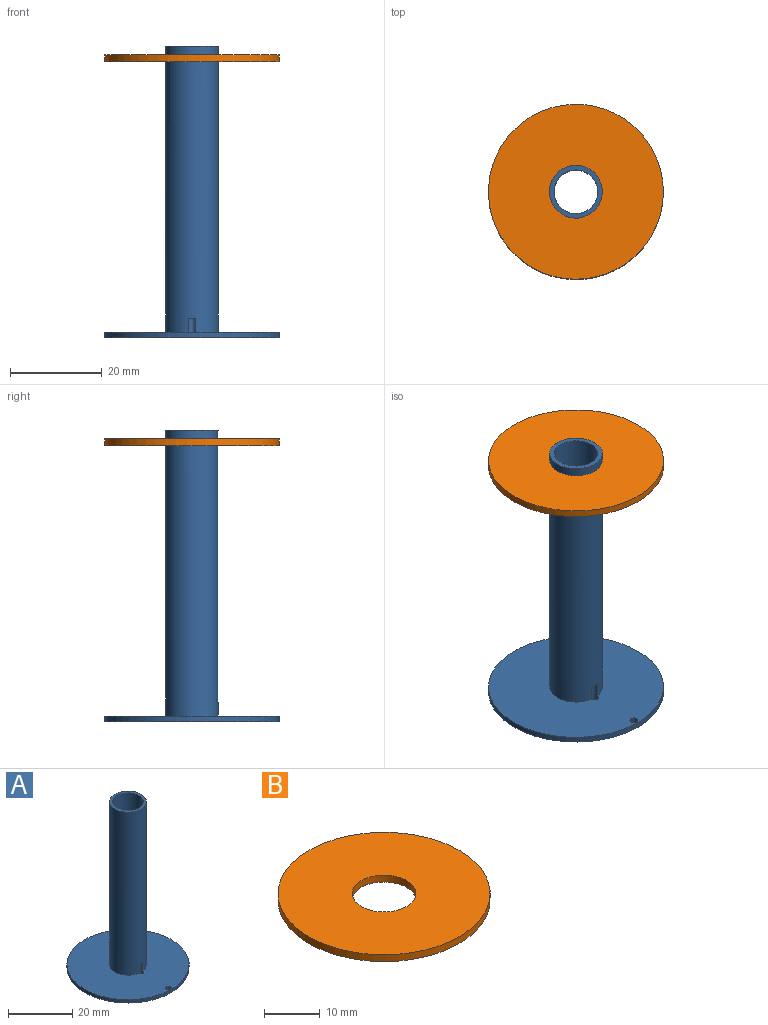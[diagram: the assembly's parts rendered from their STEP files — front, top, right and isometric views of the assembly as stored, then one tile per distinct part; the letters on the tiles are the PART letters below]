
ASSEMBLY  parts=2 mates=1
PART A: 9 faces, bbox 38.1x38.1x63.5 mm
  f0: cylinder r=19.05mm len=38.1mm, axis (0,0,-1), area 149.6mm2, adj f2,f3
  f1: cylinder r=4.75mm len=63.5mm, axis (0,0,-1), area 1895.2mm2, adj f3,f5
  f2: plane 38.1x38.1mm, normal (0,0,1), area 1032.8mm2, adj f0,f4,f6,f8
  f3: plane 38.1x38.1mm, normal (0,0,-1), area 1064.7mm2, adj f0,f1,f6,f8
  f4: cylinder r=5.75mm len=62.25mm, axis (0,0,-1), area 2243.8mm2, adj f2,f5,f6,f7
  f5: plane 11.5x11.5mm, normal (0,0,1), area 33mm2, adj f1,f4
  f6: cylinder r=0.85mm len=4.27mm, axis (0,0,1), area 14.4mm2, adj f2,f3,f4,f7
  f7: plane 1.7x0.85mm, normal (0,0,-1), area 1.1mm2, adj f4,f6
  f8: cylinder r=0.85mm len=1.7mm, axis (0,0,1), area 6.7mm2, adj f2,f3
PART B: 4 faces, bbox 38.1x38.1x1.5 mm
  f0: cylinder r=5.73mm len=11.45mm, axis (0,0,-1), area 54mm2, adj f2,f3
  f1: cylinder r=19.05mm len=38.1mm, axis (0,0,-1), area 179.5mm2, adj f2,f3
  f2: plane 38.1x38.1mm, normal (0,0,1), area 1037.1mm2, adj f0,f1
  f3: plane 38.1x38.1mm, normal (0,0,-1), area 1037.1mm2, adj f0,f1
PLACE A t=(-26.11,26.5,-3.64)mm
PLACE B t=(-26.11,26.5,56.49)mm
MATE cylindrical A.f0 <-> B.f0  axis (0,0,-1) through (-26.11,26.5,28.73)mm
